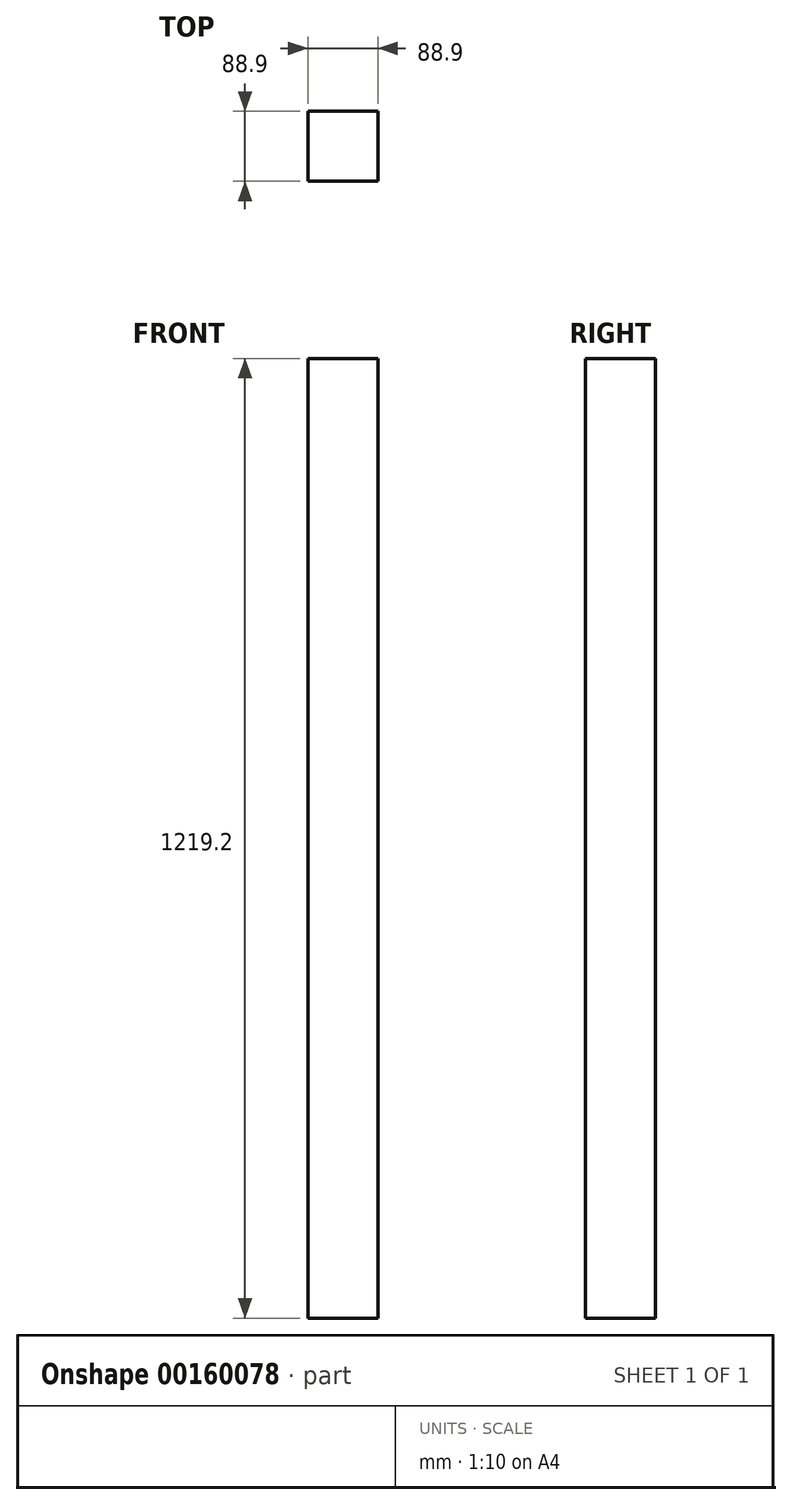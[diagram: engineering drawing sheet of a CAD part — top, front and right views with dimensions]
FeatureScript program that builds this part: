
annotation { "Feature Type Name" : "Feature", "Feature Type Description" : "" }
export const myFeature = defineFeature(function(context is Context, id is Id, definition is map)
    precondition{}
    {
        {
            var Q0;
            Q0=qCreatedBy(makeId("Top.planeOp"),FACE);
            var sketch = newSketch(context, id + "F0", { "sketchPlane" : qUnion([Q0])});
            skLineSegment(sketch, "E0.bottom", {"start": v(0, 0) * mm, "end": v(88.9, 0) * mm});
            skLineSegment(sketch, "E0.top", {"start": v(0, 88.9) * mm, "end": v(88.9, 88.9) * mm});
            skLineSegment(sketch, "E0.left", {"start": v(0, 0) * mm, "end": v(0, 88.9) * mm});
            skLineSegment(sketch, "E0.right", {"start": v(88.9, 0) * mm, "end": v(88.9, 88.9) * mm});
            skSolve(sketch);
        }
        {
            var Q0;
            Q0 = qSketchRegion(id + "F0", true);
            extrude(context, id + "F1", {"entities" : qUnion([Q0]), "depth" : 1219.2 * mm});
        }
    });
